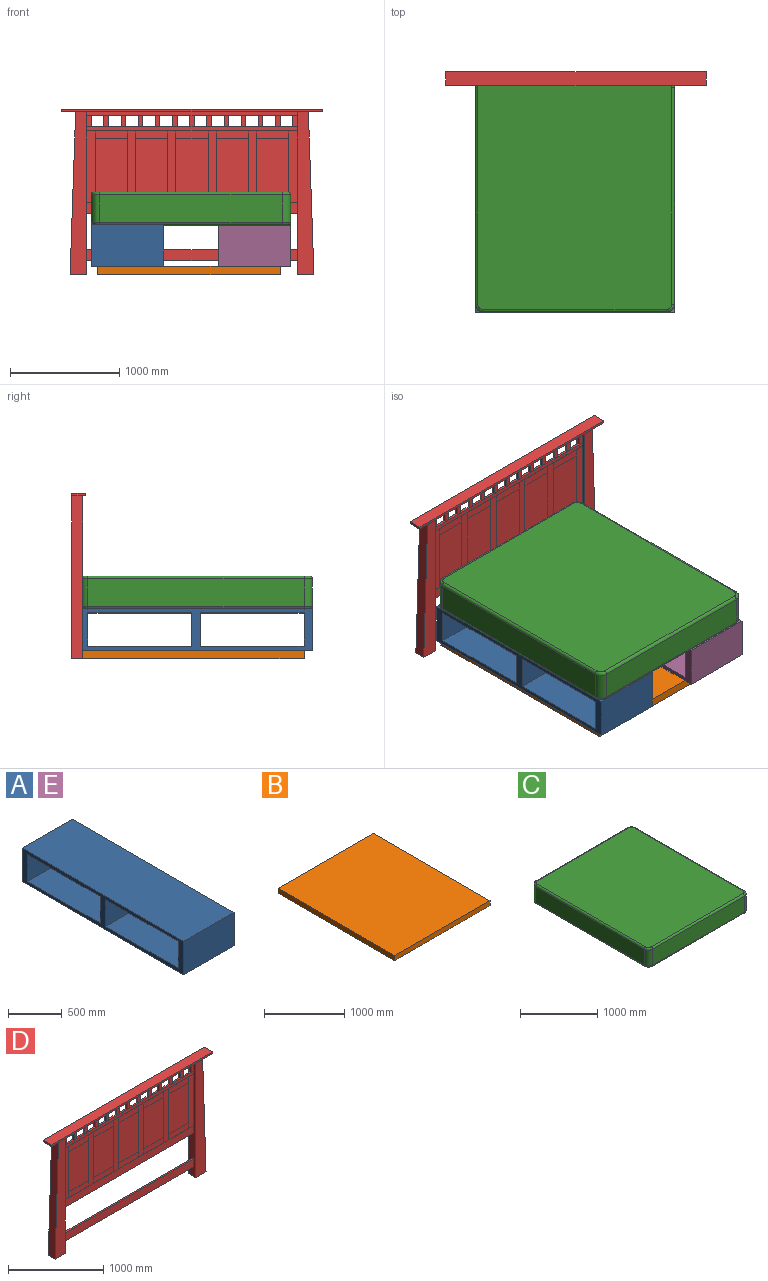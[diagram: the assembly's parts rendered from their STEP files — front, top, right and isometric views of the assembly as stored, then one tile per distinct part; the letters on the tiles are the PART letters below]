
ASSEMBLY  parts=5 mates=8
PART A: 14 faces, bbox 660.4x2133.6x381 mm
  f0: plane 2133.6x381mm, normal (1,0,0), area 232257.6mm2, adj f2,f3,f4,f5,f6,f7,f8,f9
  f1: plane 2133.6x381mm, normal (-1,0,0), area 232257.6mm2, adj f2,f3,f4,f5,f6,f7,f8,f9
  f2: plane 660.4x381mm, normal (0,1,0), area 251612.4mm2, adj f0,f1,f4,f5
  f3: plane 660.4x381mm, normal (0,-1,0), area 251612.4mm2, adj f0,f1,f4,f5
  f4: plane 2133.6x660.4mm, normal (0,0,1), area 1409029.4mm2, adj f0,f1,f2,f3
  f5: plane 2133.6x660.4mm, normal (0,0,-1), area 1409029.4mm2, adj f0,f1,f2,f3
  f6: plane 952.5x660.4mm, normal (0,0,-1), area 629031mm2, adj f0,f1,f7,f9
  f7: plane 660.4x304.8mm, normal (0,-1,0), area 201289.9mm2, adj f0,f1,f6,f8
  f8: plane 952.5x660.4mm, normal (0,0,1), area 629031mm2, adj f0,f1,f7,f9
  f9: plane 660.4x304.8mm, normal (0,1,0), area 201289.9mm2, adj f0,f1,f6,f8
  f10: plane 952.5x660.4mm, normal (0,0,-1), area 629031mm2, adj f0,f1,f11,f13
  f11: plane 660.4x304.8mm, normal (0,-1,0), area 201289.9mm2, adj f0,f1,f10,f12
  f12: plane 952.5x660.4mm, normal (0,0,1), area 629031mm2, adj f0,f1,f11,f13
  f13: plane 660.4x304.8mm, normal (0,1,0), area 201289.9mm2, adj f0,f1,f10,f12
PART B: 6 faces, bbox 1676.4x2057.4x76.2 mm
  f0: plane 1676.4x76.2mm, normal (0,1,0), area 127741.7mm2, adj f1,f3,f4,f5
  f1: plane 2057.4x76.2mm, normal (-1,0,0), area 156773.9mm2, adj f0,f2,f4,f5
  f2: plane 1676.4x76.2mm, normal (0,-1,0), area 127741.7mm2, adj f1,f3,f4,f5
  f3: plane 2057.4x76.2mm, normal (1,0,0), area 156773.9mm2, adj f0,f2,f4,f5
  f4: plane 2057.4x1676.4mm, normal (0,0,1), area 3449025.4mm2, adj f0,f1,f2,f3
  f5: plane 2057.4x1676.4mm, normal (0,0,-1), area 3449025.4mm2, adj f0,f1,f2,f3
PART C: 26 faces, bbox 1841.4x2146.2x304.8 mm
  f0: plane 1676.4x254mm, normal (0,1,0), area 425805.6mm2, adj f6,f9,f13,f21
  f1: plane 1981.2x254mm, normal (-1,0,0), area 503224.8mm2, adj f6,f7,f17,f18
  f2: plane 1676.4x254mm, normal (0,-1,0), area 425805.6mm2, adj f7,f8,f14,f22
  f3: plane 1981.2x254mm, normal (1,0,0), area 503224.8mm2, adj f8,f9,f10,f25
  f4: plane 2082.8x1778mm, normal (0,0,1), area 3701003.2mm2, adj f10,f11,f12,f13,f14,f15,f16,f17
  f5: plane 2082.8x1778mm, normal (0,0,-1), area 3701003.2mm2, adj f18,f19,f20,f21,f22,f23,f24,f25
  f6: cylinder r=76.2mm len=254mm, axis (0,0,1), area 30402.4mm2, adj f0,f1,f15,f19
  f7: cylinder r=76.2mm len=254mm, axis (0,0,-1), area 30402.4mm2, adj f1,f2,f16,f20
  f8: cylinder r=76.2mm len=254mm, axis (0,0,1), area 30402.4mm2, adj f2,f3,f12,f24
  f9: cylinder r=76.2mm len=254mm, axis (0,0,-1), area 30402.4mm2, adj f0,f3,f11,f23
  f10: cylinder r=25.4mm len=1981.2mm, axis (0,-1,0), area 79046.4mm2, adj f3,f4,f11,f12
  f11: torus R=50.8mm, axis (0,0,1), area 4197.2mm2, adj f4,f9,f10,f13
  f12: torus R=50.8mm, axis (0,0,1), area 4197.2mm2, adj f4,f8,f10,f14
  f13: cylinder r=25.4mm len=1676.4mm, axis (1,0,0), area 66885.4mm2, adj f0,f4,f11,f15
  f14: cylinder r=25.4mm len=1676.4mm, axis (-1,0,0), area 66885.4mm2, adj f2,f4,f12,f16
  f15: torus R=50.8mm, axis (0,0,1), area 4197.2mm2, adj f4,f6,f13,f17
  f16: torus R=50.8mm, axis (0,0,1), area 4197.2mm2, adj f4,f7,f14,f17
  f17: cylinder r=25.4mm len=1981.2mm, axis (0,1,0), area 79046.4mm2, adj f1,f4,f15,f16
  f18: cylinder r=25.4mm len=1981.2mm, axis (0,-1,0), area 79046.4mm2, adj f1,f5,f19,f20
  f19: torus R=50.8mm, axis (0,0,1), area 4197.2mm2, adj f5,f6,f18,f21
  f20: torus R=50.8mm, axis (0,0,1), area 4197.2mm2, adj f5,f7,f18,f22
  f21: cylinder r=25.4mm len=1676.4mm, axis (-1,0,0), area 66885.4mm2, adj f0,f5,f19,f23
  f22: cylinder r=25.4mm len=1676.4mm, axis (1,0,0), area 66885.4mm2, adj f2,f5,f20,f24
  f23: torus R=50.8mm, axis (0,0,1), area 4197.2mm2, adj f5,f9,f21,f25
  f24: torus R=50.8mm, axis (0,0,1), area 4197.2mm2, adj f5,f8,f22,f25
  f25: cylinder r=25.4mm len=1981.2mm, axis (0,1,0), area 79046.4mm2, adj f3,f5,f23,f24
PART D: 126 faces, bbox 2387.6x127x1512.9 mm
  f0: plane 514.35x294.64mm, normal (0,-1,0), area 151548.1mm2, adj f7,f8,f119,f124
  f1: plane 514.35x294.64mm, normal (0,-1,0), area 151548.1mm2, adj f9,f10,f111,f116
  f2: plane 514.35x294.64mm, normal (0,-1,0), area 151548.1mm2, adj f11,f12,f103,f108
  f3: plane 514.35x294.64mm, normal (0,-1,0), area 151548.1mm2, adj f13,f14,f95,f100
  f4: plane 514.35x294.64mm, normal (0,-1,0), area 151548.1mm2, adj f15,f16,f87,f92
  f5: plane 1930.4x38.1mm, normal (0,-1,0), area 73548.2mm2, adj f43,f44,f58,f70
  f6: plane 1930.4x95.25mm, normal (0,-1,0), area 183870.6mm2, adj f43,f44,f59,f71
  f7: plane 514.35x0.13mm, normal (-1,0,0), area 65.3mm2, adj f0,f65,f119,f124
  f8: plane 514.35x0.13mm, normal (1,0,0), area 65.3mm2, adj f0,f66,f119,f124
  f9: plane 514.35x0.13mm, normal (-1,0,0), area 65.3mm2, adj f1,f66,f111,f116
  f10: plane 514.35x0.13mm, normal (1,0,0), area 65.3mm2, adj f1,f67,f111,f116
  f11: plane 514.35x0.13mm, normal (-1,0,0), area 65.3mm2, adj f2,f67,f103,f108
  f12: plane 514.35x0.13mm, normal (1,0,0), area 65.3mm2, adj f2,f68,f103,f108
  f13: plane 514.35x0.13mm, normal (-1,0,0), area 65.3mm2, adj f3,f68,f95,f100
  f14: plane 514.35x0.13mm, normal (1,0,0), area 65.3mm2, adj f3,f69,f95,f100
  f15: plane 514.35x0.13mm, normal (-1,0,0), area 65.3mm2, adj f4,f69,f87,f92
  f16: plane 514.35x0.13mm, normal (1,0,0), area 65.3mm2, adj f4,f72,f87,f92
  f17: plane 103.19x22.1mm, normal (1,0,0), area 2280.2mm2, adj f57,f58,f60,f75
  f18: plane 103.19x22.1mm, normal (-1,0,0), area 2280.2mm2, adj f57,f58,f60,f76
  f19: plane 103.19x22.1mm, normal (1,0,0), area 2280.2mm2, adj f57,f58,f60,f84
  f20: plane 103.19x22.1mm, normal (-1,0,0), area 2280.2mm2, adj f57,f58,f60,f83
  f21: plane 103.19x22.1mm, normal (1,0,0), area 2280.2mm2, adj f57,f58,f60,f81
  f22: plane 103.19x22.1mm, normal (-1,0,0), area 2280.2mm2, adj f57,f58,f60,f82
  f23: plane 103.19x22.1mm, normal (1,0,0), area 2280.2mm2, adj f57,f58,f60,f77
  f24: plane 103.19x22.1mm, normal (1,0,0), area 2280.2mm2, adj f57,f58,f60,f82
  f25: plane 103.19x22.1mm, normal (1,0,0), area 2280.2mm2, adj f57,f58,f60,f85
  f26: plane 103.19x22.1mm, normal (1,0,0), area 2280.2mm2, adj f57,f58,f60,f83
  f27: plane 103.19x22.1mm, normal (1,0,0), area 2280.2mm2, adj f57,f58,f60,f80
  f28: plane 103.19x22.1mm, normal (-1,0,0), area 2280.2mm2, adj f57,f58,f60,f81
  f29: plane 103.19x22.1mm, normal (1,0,0), area 2280.2mm2, adj f57,f58,f60,f76
  f30: plane 103.19x22.1mm, normal (1,0,0), area 2280.2mm2, adj f57,f58,f60,f78
  f31: plane 103.19x22.1mm, normal (1,0,0), area 2280.2mm2, adj f57,f58,f60,f79
  f32: plane 103.19x22.1mm, normal (1,0,0), area 2280.2mm2, adj f57,f58,f60,f73
  f33: plane 103.19x22.1mm, normal (-1,0,0), area 2280.2mm2, adj f57,f58,f60,f75
  f34: plane 103.19x22.1mm, normal (-1,0,0), area 2280.2mm2, adj f57,f58,f60,f78
  f35: plane 103.19x22.1mm, normal (-1,0,0), area 2280.2mm2, adj f57,f58,f60,f85
  f36: plane 103.19x22.1mm, normal (-1,0,0), area 2280.2mm2, adj f57,f58,f60,f84
  f37: plane 103.19x22.1mm, normal (-1,0,0), area 2280.2mm2, adj f57,f58,f60,f74
  f38: plane 103.19x22.1mm, normal (-1,0,0), area 2280.2mm2, adj f57,f58,f60,f77
  f39: plane 103.19x22.1mm, normal (-1,0,0), area 2280.2mm2, adj f57,f58,f60,f79
  f40: plane 103.19x22.1mm, normal (-1,0,0), area 2280.2mm2, adj f57,f58,f60,f80
  f41: plane 1930.4x31.75mm, normal (0,-1,0), area 61290.2mm2, adj f43,f44,f51,f57
  f42: plane 1930.4x50.8mm, normal (0,0,-1), area 98064.3mm2, adj f43,f44,f55,f60
  f43: plane 1490.66x101.6mm, normal (1,0,0), area 128650.1mm2, adj f5,f6,f41,f42,f45,f48,f51,f55
  f44: plane 1490.66x101.6mm, normal (-1,0,0), area 128650.1mm2, adj f5,f6,f41,f42,f49,f51,f54,f55
  f45: plane 1490.66x152.4mm, normal (0,-1,0), area 189314.1mm2, adj f43,f47,f48,f51
  f46: plane 127x22.23mm, normal (-1,0,0), area 2822.6mm2, adj f51,f53,f55,f56
  f47: plane 1490.66x101.6mm, normal (-1,0,0.03), area 151539.2mm2, adj f45,f48,f51,f55
  f48: plane 152.4x101.6mm, normal (0,0,-1), area 15483.8mm2, adj f43,f45,f47,f55
  f49: plane 152.4x101.6mm, normal (0,0,-1), area 15483.8mm2, adj f44,f50,f54,f55
  f50: plane 1490.66x101.6mm, normal (1,0,0.03), area 151539.2mm2, adj f49,f51,f54,f55
  f51: plane 2387.6x127mm, normal (0,0,-1), area 141612.6mm2, adj f41,f43,f44,f45,f46,f47,f50,f52
  f52: plane 127x22.23mm, normal (1,0,0), area 2822.6mm2, adj f51,f53,f55,f56
  f53: plane 2387.6x127mm, normal (0,0,1), area 303225.2mm2, adj f46,f52,f55,f56
  f54: plane 1490.66x152.4mm, normal (0,-1,0), area 189314.1mm2, adj f44,f49,f50,f51
  f55: plane 2387.6x1512.89mm, normal (0,1,0), area 431692.7mm2, adj f42,f43,f44,f46,f47,f48,f49,f50
  f56: plane 2387.6x22.23mm, normal (0,-1,0), area 53064.4mm2, adj f46,f51,f52,f53
  f57: plane 1930.4x22.23mm, normal (0,0,-1), area 31468.5mm2, adj f17,f18,f19,f20,f21,f22,f23,f24
  f58: plane 1930.4x22.23mm, normal (0,0,1), area 31468.5mm2, adj f5,f17,f18,f19,f20,f21,f22,f23
  f59: plane 1930.4x22.23mm, normal (0,0,-1), area 42903.1mm2, adj f6,f43,f44,f60
  f60: plane 1930.4x928.69mm, normal (0,1,0), area 1646939.9mm2, adj f17,f18,f19,f20,f21,f22,f23,f24
  f61: plane 1930.4x22.23mm, normal (0,0,-1), area 42903.1mm2, adj f43,f44,f63,f64
  f62: plane 1930.4x22.23mm, normal (0,0,1), area 42903.1mm2, adj f43,f44,f63,f64
  f63: plane 1930.4x101.6mm, normal (0,-1,0), area 196128.6mm2, adj f43,f44,f61,f62
  f64: plane 1930.4x101.6mm, normal (0,1,0), area 196128.6mm2, adj f43,f44,f61,f62
  f65: plane 660.4x76.2mm, normal (0,-1,0), area 50322.5mm2, adj f7,f43,f70,f71,f118,f122
  f66: plane 660.4x76.2mm, normal (0,-1,0), area 50322.5mm2, adj f8,f9,f70,f71,f110,f114,f120,f123
  f67: plane 660.4x76.2mm, normal (0,-1,0), area 50322.5mm2, adj f10,f11,f70,f71,f102,f106,f112,f115
  f68: plane 660.4x76.2mm, normal (0,-1,0), area 50322.5mm2, adj f12,f13,f70,f71,f94,f98,f104,f107
  f69: plane 660.4x76.2mm, normal (0,-1,0), area 50322.5mm2, adj f14,f15,f70,f71,f86,f90,f96,f99
  f70: plane 1930.4x0.15mm, normal (0,0,-1), area 282.6mm2, adj f5,f43,f44,f65,f66,f67,f68,f69
  f71: plane 1930.4x0.15mm, normal (0,0,1), area 282.6mm2, adj f6,f43,f44,f65,f66,f67,f68,f69
  f72: plane 660.4x76.2mm, normal (0,-1,0), area 50322.5mm2, adj f16,f44,f70,f71,f88,f91
  f73: plane 103.19x39.69mm, normal (0,-1,0), area 4095.3mm2, adj f32,f43,f57,f58
  f74: plane 103.19x39.69mm, normal (0,-1,0), area 4095.3mm2, adj f37,f44,f57,f58
  f75: plane 103.19x39.69mm, normal (0,-1,0), area 4095.3mm2, adj f17,f33,f57,f58
  f76: plane 103.19x39.69mm, normal (0,-1,0), area 4095.3mm2, adj f18,f29,f57,f58
  f77: plane 103.19x39.69mm, normal (0,-1,0), area 4095.3mm2, adj f23,f38,f57,f58
  f78: plane 103.19x39.69mm, normal (0,-1,0), area 4095.3mm2, adj f30,f34,f57,f58
  f79: plane 103.19x40.45mm, normal (0,-1,0), area 4173.5mm2, adj f31,f39,f57,f58
  f80: plane 103.19x39.69mm, normal (0,-1,0), area 4095.3mm2, adj f27,f40,f57,f58
  f81: plane 103.19x40.45mm, normal (0,-1,0), area 4173.5mm2, adj f21,f28,f57,f58
  f82: plane 103.19x39.69mm, normal (0,-1,0), area 4095.3mm2, adj f22,f24,f57,f58
  f83: plane 103.19x39.69mm, normal (0,-1,0), area 4095.3mm2, adj f20,f26,f57,f58
  f84: plane 103.19x39.69mm, normal (0,-1,0), area 4095.3mm2, adj f19,f36,f57,f58
  f85: plane 103.19x39.69mm, normal (0,-1,0), area 4095.3mm2, adj f25,f35,f57,f58
  f86: plane 73.03x0.03mm, normal (1,0,0), area 1.9mm2, adj f69,f70,f87,f89
  f87: plane 294.64x0.15mm, normal (0,0,1), area 44.9mm2, adj f4,f15,f16,f86,f88,f89
  f88: plane 73.03x0.03mm, normal (-1,0,0), area 1.9mm2, adj f70,f72,f87,f89
  f89: plane 294.64x73.03mm, normal (0,-1,0), area 21516.1mm2, adj f70,f86,f87,f88
  f90: plane 73.03x0.03mm, normal (1,0,0), area 1.9mm2, adj f69,f71,f92,f93
  f91: plane 73.03x0.03mm, normal (-1,0,0), area 1.9mm2, adj f71,f72,f92,f93
  f92: plane 294.64x0.15mm, normal (0,0,-1), area 44.9mm2, adj f4,f15,f16,f90,f91,f93
  f93: plane 294.64x73.03mm, normal (0,-1,0), area 21516.1mm2, adj f71,f90,f91,f92
  f94: plane 73.03x0.03mm, normal (1,0,0), area 1.9mm2, adj f68,f70,f95,f97
  f95: plane 294.64x0.15mm, normal (0,0,1), area 44.9mm2, adj f3,f13,f14,f94,f96,f97
  f96: plane 73.03x0.03mm, normal (-1,0,0), area 1.9mm2, adj f69,f70,f95,f97
  f97: plane 294.64x73.03mm, normal (0,-1,0), area 21516.1mm2, adj f70,f94,f95,f96
  f98: plane 73.03x0.03mm, normal (1,0,0), area 1.9mm2, adj f68,f71,f100,f101
  f99: plane 73.03x0.03mm, normal (-1,0,0), area 1.9mm2, adj f69,f71,f100,f101
  f100: plane 294.64x0.15mm, normal (0,0,-1), area 44.9mm2, adj f3,f13,f14,f98,f99,f101
  f101: plane 294.64x73.03mm, normal (0,-1,0), area 21516.1mm2, adj f71,f98,f99,f100
  f102: plane 73.03x0.03mm, normal (1,0,0), area 1.9mm2, adj f67,f70,f103,f105
  f103: plane 294.64x0.15mm, normal (0,0,1), area 44.9mm2, adj f2,f11,f12,f102,f104,f105
  f104: plane 73.03x0.03mm, normal (-1,0,0), area 1.9mm2, adj f68,f70,f103,f105
  f105: plane 294.64x73.03mm, normal (0,-1,0), area 21516.1mm2, adj f70,f102,f103,f104
  f106: plane 73.03x0.03mm, normal (1,0,0), area 1.9mm2, adj f67,f71,f108,f109
  f107: plane 73.03x0.03mm, normal (-1,0,0), area 1.9mm2, adj f68,f71,f108,f109
  f108: plane 294.64x0.15mm, normal (0,0,-1), area 44.9mm2, adj f2,f11,f12,f106,f107,f109
  f109: plane 294.64x73.03mm, normal (0,-1,0), area 21516.1mm2, adj f71,f106,f107,f108
  f110: plane 73.03x0.03mm, normal (1,0,0), area 1.9mm2, adj f66,f70,f111,f113
  f111: plane 294.64x0.15mm, normal (0,0,1), area 44.9mm2, adj f1,f9,f10,f110,f112,f113
  f112: plane 73.03x0.03mm, normal (-1,0,0), area 1.9mm2, adj f67,f70,f111,f113
  f113: plane 294.64x73.03mm, normal (0,-1,0), area 21516.1mm2, adj f70,f110,f111,f112
  f114: plane 73.03x0.03mm, normal (1,0,0), area 1.9mm2, adj f66,f71,f116,f117
  f115: plane 73.03x0.03mm, normal (-1,0,0), area 1.9mm2, adj f67,f71,f116,f117
  f116: plane 294.64x0.15mm, normal (0,0,-1), area 44.9mm2, adj f1,f9,f10,f114,f115,f117
  f117: plane 294.64x73.03mm, normal (0,-1,0), area 21516.1mm2, adj f71,f114,f115,f116
  f118: plane 73.03x0.03mm, normal (1,0,0), area 1.9mm2, adj f65,f70,f119,f121
  f119: plane 294.64x0.15mm, normal (0,0,1), area 44.9mm2, adj f0,f7,f8,f118,f120,f121
  f120: plane 73.03x0.03mm, normal (-1,0,0), area 1.9mm2, adj f66,f70,f119,f121
  f121: plane 294.64x73.03mm, normal (0,-1,0), area 21516.1mm2, adj f70,f118,f119,f120
  f122: plane 73.03x0.03mm, normal (1,0,0), area 1.9mm2, adj f65,f71,f124,f125
  f123: plane 73.03x0.03mm, normal (-1,0,0), area 1.9mm2, adj f66,f71,f124,f125
  f124: plane 294.64x0.15mm, normal (0,0,-1), area 44.9mm2, adj f0,f7,f8,f122,f123,f125
  f125: plane 294.64x73.03mm, normal (0,-1,0), area 21516.1mm2, adj f71,f122,f123,f124
PART E: same geometry as A
PLACE A t=(-100.12,-89.27,-59.23)mm
PLACE B t=(128.62,-89.27,-135.43)mm
PLACE C t=(-267.88,-89.27,316.13)mm
PLACE D t=(157.09,-67.04,-135.43)mm fixed
PLACE E t=(1060.56,-89.27,-64.87)mm
MATE planar B.f0 <-> D.f63  axis (0,1,0) through (128.62,-89.27,-97.33)mm
MATE planar C.f3 <-> E.f0  axis (1,0,0) through (1060.56,-1156.07,468.53)mm
MATE planar B.f5 <-> D.f49  axis (0,0,-1) through (128.62,-1117.97,-135.43)mm
MATE parallel E.f5 <-> B.f4  axis (0,0,-1) through (730.36,-1156.07,-64.87)mm
MATE planar B.f0 <-> E.f2  axis (0,1,0) through (128.62,-89.27,-97.33)mm
MATE planar C.f5 <-> E.f4  axis (0,0,-1) through (146.16,-1156.07,316.13)mm
MATE planar A.f5 <-> B.f4  axis (0,0,-1) through (-430.32,-1156.07,-59.23)mm
MATE planar A.f2 <-> B.f0  axis (0,1,0) through (-430.32,-89.27,131.27)mm
